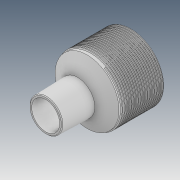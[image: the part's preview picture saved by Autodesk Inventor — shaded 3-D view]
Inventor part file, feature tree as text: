
AUTODESK INVENTOR PART (.ipt)
format: ipt  version: 2020 (Build 240168000, 168)  size: 891,392 bytes
history: native  units: mm
features: sketch x16, extrude x9, chamfer x8, revolve x5, helix x2, plane x2, split x1, projected_geometry x1
ambient origin geometry x8: Origin, YZ Plane, XZ Plane, XY Plane, X Axis, Y Axis, Z Axis, Center Point
bodies: Solid1 (feature_tree)
feature tree (44):
  extrude  "Extrusion1"  Depth=2.0mm
  chamfer  "Chamfer1"  Distance=2.0mm
  revolve  "Revolution1"  [1 undecoded]
  extrude  "Extrusion2"  Depth=18.75mm
  sketch  "Sketch6"  dims[d17=1.6mm]
  helix  "Coil2"  [1 undecoded]
  chamfer  "Chamfer4"  Distance=10.0mm
  chamfer  "Chamfer5"  Distance=0.65mm Angle=45.0deg
  extrude  "Extrusion4"  Depth=42.0mm
  extrude  "Extrusion6"  Depth=2.65mm
  extrude  "Extrusion7"  Depth=1.2mm
  helix  "Coil3"  [1 undecoded]
  extrude  "Extrusion8"  Depth=10.0mm TaperAngle=0.0deg
  revolve  "Revolution2"  [1 undecoded]
  extrude  "Extrusion9"  Depth=10.0mm
  plane  "Work Plane3"
  split  "Split2"
  revolve  "Revolution3"  [1 undecoded]
  sketch  "Sketch17"  dims[d54=0.65mm d55=4.0mm d56=45.0deg d57=42.0mm]
  revolve  "Revolution6"  [1 undecoded]
  plane  "Work Plane4"
  extrude  "Extrusion10"  Depth=10.0mm TaperAngle=0.0deg
  chamfer  "Chamfer9"  Angle=135.0deg  [1 undecoded]
  chamfer  "Chamfer10"  Angle=90.0deg  [1 undecoded]
  revolve  "Revolution8"  [1 undecoded]
  chamfer  "Chamfer12"  [1 undecoded]
  chamfer  "Chamfer13"  Distance=21.0mm
  extrude  "Extrusion11"  Depth=10.0mm
  chamfer  "Chamfer14"  Distance=1.6mm
  sketch  "Sketch1"  dims[d0=18.0mm d1=2.0mm d2=2.0mm d3=0.0mm]
  sketch  "Sketch4"  dims[d4=2.0mm d5=2.0mm d6=45.0deg d10=12.25mm]
  sketch  "Sketch5"  dims[d11=8.0mm d12=18.75mm d14=1.5mm]
  projected_geometry  "Projected Loop1"
  sketch  "Sketch8"  dims[d18=90.0deg d19=10.0mm d20=0.0mm]
  sketch  "Sketch9"  dims[d21=1.0mm]
  sketch  "Sketch10"  dims[d22=1.0mm]
  sketch  "Sketch11"  dims[d23=1.5mm]
  sketch  "Sketch12"  dims[d24=0.8mm]
  sketch  "Sketch13"  dims[d42=0.1mm]
  sketch  "Sketch14"  dims[d43=1.5mm]
  sketch  "Sketch15"  dims[d44=6.0mm d45=10.0mm d46=0.0mm d47=90.0deg d48=90.0deg d49=0.0mm d50=0.0mm d51=0.65mm d52=4.0mm d53=45.0deg]
  sketch  "Sketch18"  dims[d58=28.0mm d59=0.0mm d60=2.65mm]
  sketch  "Sketch19"  dims[d61=1.2mm d62=1.2mm d65=12.0mm d66=0.0mm]
  sketch  "Sketch20"  dims[d67=30.0mm d68=3.0mm d69=0.0mm d74=1.0mm d75=0.65mm d76=1.5mm d77=28.0mm d78=10.0mm d79=0.0mm d80=90.0deg d81=90.0deg d82=0.0mm d83=0.0mm d84=45.0mm d85=20.0mm d86=0.0mm d87=135.0deg d88=90.0deg d90=0.7mm d91=0.0mm d92=0.0mm d95=21.0mm d96=10.81mm d97=1.6mm d98=1.6mm d99=6.981317mm d100=90.0deg d101=0.75mm d102=1.4mm d103=18.0mm d104=2.4mm d105=2.0mm d109=15.0mm d116=90.0deg d117=45.0deg d120=10.0mm d121=2.0mm d122=12.0mm d123=0.0mm d124=0.0mm d131=0.5mm d132=2.0mm d133=45.0deg d134=17.0mm d135=13.0mm d136=3.0mm d137=2.0mm d138=45.0deg d142=90.0deg d143=1.8mm d144=2.4mm d145=45.0deg d146=2.15mm d147=2.0mm d148=45.0deg d149=0.75mm d150=0.75mm d151=8.0mm d152=10.0mm d153=0.0mm d154=15.0mm d155=2.0mm d156=45.0deg d157=15.0mm d158=11.185mm d70=0.5mm d71=0.872665mm d72=0.5mm d73=0.872665mm d89=0.5mm]
note: 10 required parameter values undecoded (feature->parameter linkage not recoverable at this tier; creation-order binding heuristic only, values carry confidence <= 0.55)